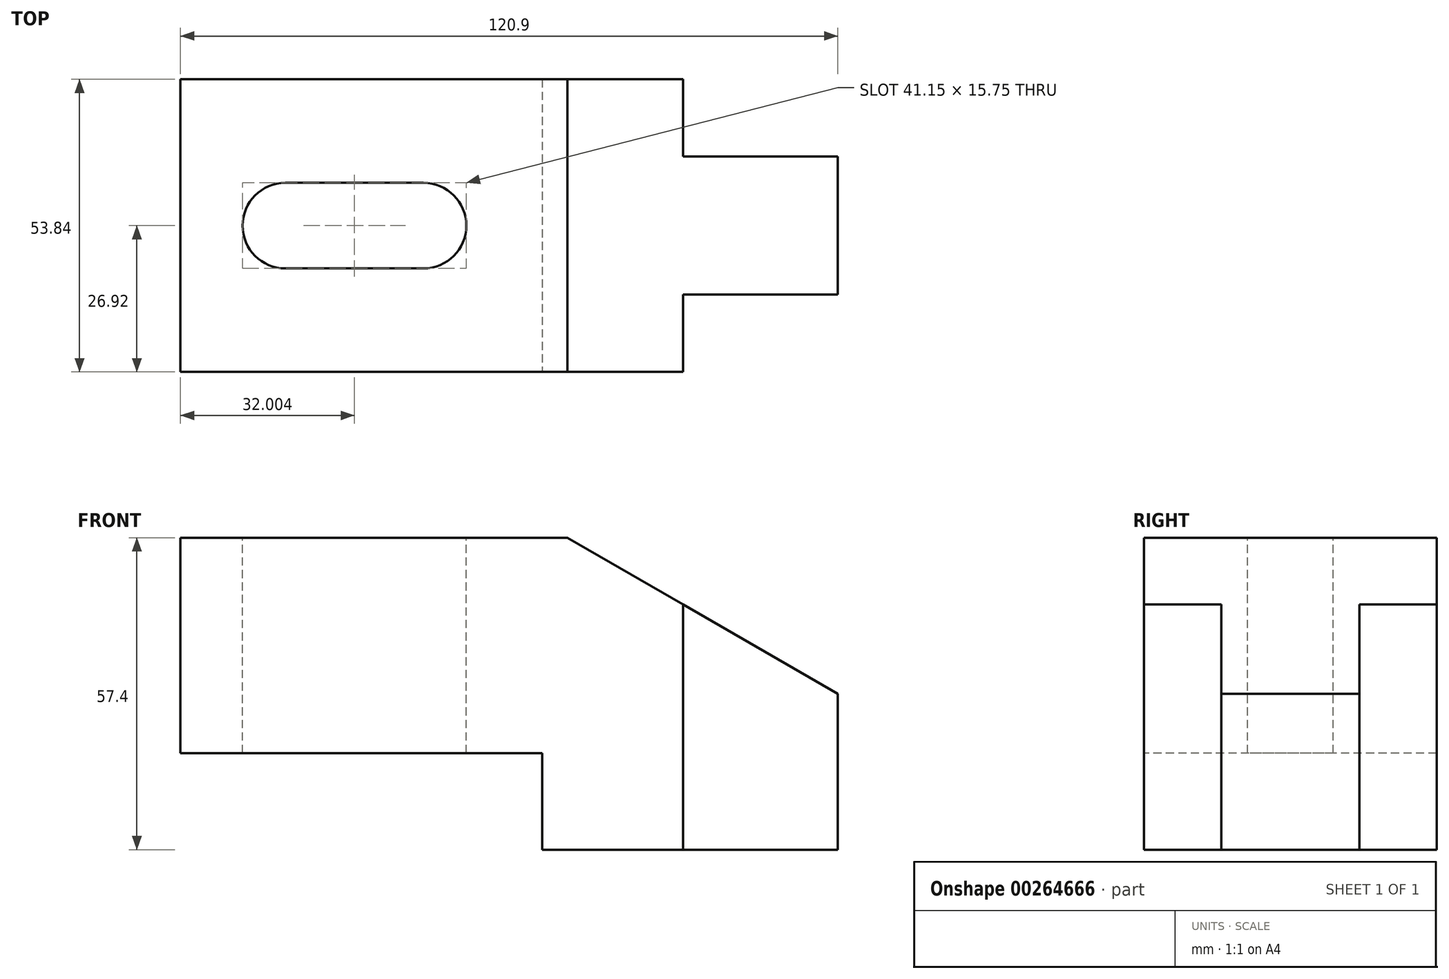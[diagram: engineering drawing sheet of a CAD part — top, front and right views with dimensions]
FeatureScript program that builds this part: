
annotation { "Feature Type Name" : "Feature", "Feature Type Description" : "" }
export const myFeature = defineFeature(function(context is Context, id is Id, definition is map)
    precondition{}
    {
        {
            var Q0;
            Q0=qCreatedBy(makeId("Front.planeOp"),FACE);
            var sketch = newSketch(context, id + "F0", { "sketchPlane" : qUnion([Q0])});
            skLineSegment(sketch, "E0.bottom", {"start": v(0, 0) * mm, "end": v(120.9, 0) * mm});
            skLineSegment(sketch, "E0.top", {"start": v(0, 57.4) * mm, "end": v(120.9, 57.4) * mm});
            skLineSegment(sketch, "E0.left", {"start": v(0, 0) * mm, "end": v(0, 57.4) * mm});
            skLineSegment(sketch, "E0.right", {"start": v(120.9, 0) * mm, "end": v(120.9, 57.4) * mm});
            skSolve(sketch);
        }
        {
            var Q0;
            Q0=makeQuery(id+"F0.imprint","IMPRINT",FACE,{"disambiguationData":[TD([[makeQuery(id+"F0.imprint","IMPRINT",EDGE,{"derivedFrom":sQuery(id+"F0.wireOp",EDGE,"E0.bottom")}),1.0]])]});
            extrude(context, id + "F1", {"entities" : qUnion([Q0]), "endBound" : BoundingType.SYMMETRIC, "depth" : 53.85 * mm});
        }
        {
            var Q0;
            Q0=makeQuery(id+"F1.opExtrude","CAP_FACE",FACE,{"disambiguationData":[OSD([sQuery(id+"F0.wireOp",EDGE,"E0.bottom"),sQuery(id+"F0.wireOp",EDGE,"E0.top"),sQuery(id+"F0.wireOp",EDGE,"E0.left"),sQuery(id+"F0.wireOp",EDGE,"E0.right")])],"isStart":false});
            var sketch = newSketch(context, id + "F2", { "sketchPlane" : qUnion([Q0])});
            skLineSegment(sketch, "E1.bottom", {"start": v(0, 0) * mm, "end": v(66.55, 0) * mm});
            skLineSegment(sketch, "E1.top", {"start": v(0, 17.78) * mm, "end": v(66.55, 17.78) * mm});
            skLineSegment(sketch, "E1.left", {"start": v(0, 0) * mm, "end": v(0, 17.78) * mm});
            skLineSegment(sketch, "E1.right", {"start": v(66.55, 0) * mm, "end": v(66.55, 17.78) * mm});
            skSolve(sketch);
        }
        {
            var Q0;
            Q0=makeQuery(id+"F2.imprint","IMPRINT",FACE,{"disambiguationData":[TD([[makeQuery(id+"F2.imprint","IMPRINT",EDGE,{"derivedFrom":sQuery(id+"F2.wireOp",EDGE,"E1.bottom")}),1.0]])]});
            extrude(context, id + "F3", {"entities" : qUnion([Q0]), "operationType" : NewBodyOperationType.REMOVE, "endBound" : BoundingType.THROUGH_ALL, "oppositeDirection" : true, "depth" : 25.4 * mm});
        }
        {
            var Q0;
            Q0=makeQuery(id+"F1.opExtrude","CAP_FACE",FACE,{"disambiguationData":[OSD([sQuery(id+"F0.wireOp",EDGE,"E0.bottom"),sQuery(id+"F0.wireOp",EDGE,"E0.top"),sQuery(id+"F0.wireOp",EDGE,"E0.left"),sQuery(id+"F0.wireOp",EDGE,"E0.right")])],"isStart":false});
            var sketch = newSketch(context, id + "F4", { "sketchPlane" : qUnion([Q0])});
            skLineSegment(sketch, "E2", {"start": v(120.9, 57.4) * mm, "end": v(71.2, 57.4) * mm});
            skLineSegment(sketch, "E3", {"start": v(71.2, 57.4) * mm, "end": v(120.9, 28.7) * mm});
            skLineSegment(sketch, "E4", {"start": v(120.9, 28.7) * mm, "end": v(120.9, 57.4) * mm});
            skSolve(sketch);
        }
        {
            var Q0;
            Q0=makeQuery(id+"F4.imprint","IMPRINT",FACE,{"disambiguationData":[TD([[makeQuery(id+"F4.imprint","IMPRINT",EDGE,{"derivedFrom":sQuery(id+"F4.wireOp",EDGE,"E2")}),-1.0]])]});
            extrude(context, id + "F5", {"entities" : qUnion([Q0]), "operationType" : NewBodyOperationType.REMOVE, "endBound" : BoundingType.THROUGH_ALL, "oppositeDirection" : true, "depth" : 25.4 * mm});
        }
        {
            var Q0;
            Q0=makeQuery(id+"F1.opExtrude","SWEPT_FACE",FACE,{"disambiguationData":[OSD([sQuery(id+"F0.wireOp",EDGE,"E0.top")])]});
            var sketch = newSketch(context, id + "F6", { "sketchPlane" : qUnion([Q0])});
            skLineSegment(sketch, "E5.bottom", {"start": v(120.9, -26.92) * mm, "end": v(92.46, -26.92) * mm});
            skLineSegment(sketch, "E5.top", {"start": v(120.9, -12.7) * mm, "end": v(92.46, -12.7) * mm});
            skLineSegment(sketch, "E5.left", {"start": v(120.9, -26.92) * mm, "end": v(120.9, -12.7) * mm});
            skLineSegment(sketch, "E5.right", {"start": v(92.46, -26.92) * mm, "end": v(92.46, -12.7) * mm});
            skLineSegment(sketch, "E6.bottom", {"start": v(120.9, 26.92) * mm, "end": v(92.46, 26.92) * mm});
            skLineSegment(sketch, "E6.top", {"start": v(120.9, 12.7) * mm, "end": v(92.46, 12.7) * mm});
            skLineSegment(sketch, "E6.left", {"start": v(120.9, 26.92) * mm, "end": v(120.9, 12.7) * mm});
            skLineSegment(sketch, "E6.right", {"start": v(92.46, 26.92) * mm, "end": v(92.46, 12.7) * mm});
            skSolve(sketch);
        }
        {
            var Q0;
            Q0=makeQuery(id+"F6.imprint","IMPRINT",FACE,{"disambiguationData":[TD([[makeQuery(id+"F6.imprint","IMPRINT",EDGE,{"derivedFrom":sQuery(id+"F6.wireOp",EDGE,"E5.bottom")}),-1.0]])]});
            var Q1;
            Q1=makeQuery(id+"F6.imprint","IMPRINT",FACE,{"disambiguationData":[TD([[makeQuery(id+"F6.imprint","IMPRINT",EDGE,{"derivedFrom":sQuery(id+"F6.wireOp",EDGE,"E6.bottom")}),1.0]])]});
            extrude(context, id + "F7", {"entities" : qUnion([Q0, Q1]), "operationType" : NewBodyOperationType.REMOVE, "endBound" : BoundingType.THROUGH_ALL, "oppositeDirection" : true, "depth" : 25.4 * mm});
        }
        {
            var Q0;
            Q0=makeQuery(id+"F1.opExtrude","SWEPT_FACE",FACE,{"disambiguationData":[OSD([sQuery(id+"F0.wireOp",EDGE,"E0.top")])]});
            var sketch = newSketch(context, id + "F8", { "sketchPlane" : qUnion([Q0])});
            skArc(sketch, "E7", {"start": v(19.3, 7.87) * mm, "mid": v(11.43, 0) * mm, "end": v(19.3, -7.87) * mm});
            skArc(sketch, "E8", {"start": v(44.7, -7.87) * mm, "mid": v(52.58, 0) * mm, "end": v(44.7, 7.87) * mm});
            skLineSegment(sketch, "E9", {"start": v(19.3, 7.87) * mm, "end": v(44.7, 7.87) * mm});
            skLineSegment(sketch, "E10", {"start": v(19.3, -7.87) * mm, "end": v(44.7, -7.87) * mm});
            skLineSegment(sketch, "E11", {"start": v(19.3, 0) * mm, "end": v(44.7, 0) * mm, "construction": true});
            skPoint(sketch, "E12", {"position": v(32, 0) * mm});
            skSolve(sketch);
        }
        {
            var Q0;
            Q0 = qSketchRegion(id + "F8", true);
            extrude(context, id + "F9", {"entities" : qUnion([Q0]), "operationType" : NewBodyOperationType.REMOVE, "endBound" : BoundingType.THROUGH_ALL, "oppositeDirection" : true, "depth" : 25.4 * mm});
        }
    });
